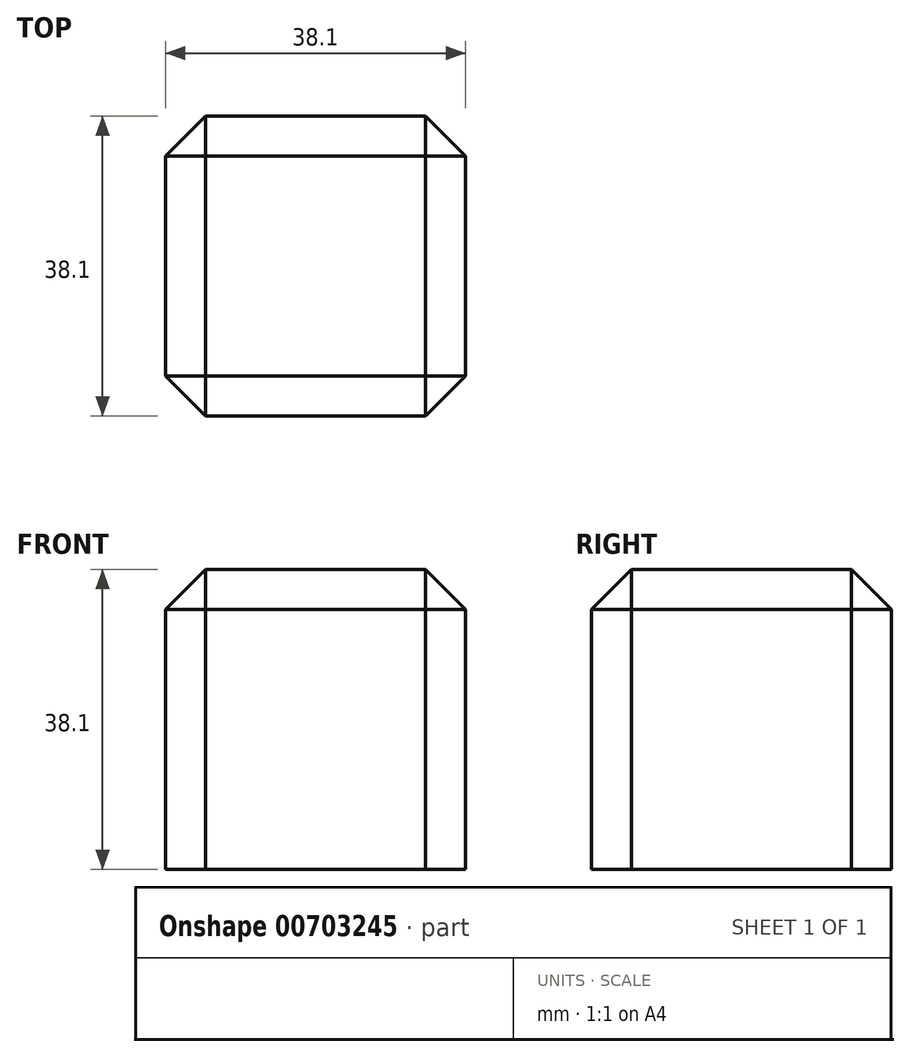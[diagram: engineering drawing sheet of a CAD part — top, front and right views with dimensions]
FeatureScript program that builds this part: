
annotation { "Feature Type Name" : "Feature", "Feature Type Description" : "" }
export const myFeature = defineFeature(function(context is Context, id is Id, definition is map)
    precondition{}
    {
        {
            var Q0;
            Q0=qCreatedBy(makeId("Front.planeOp"),FACE);
            var sketch = newSketch(context, id + "F0", { "sketchPlane" : qUnion([Q0])});
            skLineSegment(sketch, "E0.bottom", {"start": v(19.05, 19.05) * mm, "end": v(-19.05, 19.05) * mm});
            skLineSegment(sketch, "E0.top", {"start": v(19.05, -19.05) * mm, "end": v(-19.05, -19.05) * mm});
            skLineSegment(sketch, "E0.left", {"start": v(19.05, 19.05) * mm, "end": v(19.05, -19.05) * mm});
            skLineSegment(sketch, "E0.right", {"start": v(-19.05, 19.05) * mm, "end": v(-19.05, -19.05) * mm});
            skPoint(sketch, "E0.middle", {"position": v(0, 0) * mm});
            skSolve(sketch);
        }
        {
            var Q0;
            Q0=makeQuery(id+"F0.imprint","IMPRINT",FACE,{"disambiguationData":[TD([[makeQuery(id+"F0.imprint","IMPRINT",EDGE,{"derivedFrom":sQuery(id+"F0.wireOp",EDGE,"E0.bottom")}),1.0]])]});
            extrude(context, id + "F1", {"entities" : qUnion([Q0]), "depth" : 38.1 * mm, "offsetDistance" : 25.4 * mm});
        }
        {
            var Q0;
            Q0=makeQuery(id+"F1.opExtrude","CAP_EDGE",EDGE,{"disambiguationData":[OSD([sQuery(id+"F0.wireOp",EDGE,"E0.bottom")])],"isStart":false});
            var Q1;
            Q1=makeQuery(id+"F1.opExtrude","SWEPT_EDGE",EDGE,{"disambiguationData":[OSD([sQuery(id+"F0.wireOp",EDGE,"E0.bottom"),sQuery(id+"F0.wireOp",EDGE,"E0.right")])]});
            var Q2;
            Q2=makeQuery(id+"F1.opExtrude","CAP_EDGE",EDGE,{"disambiguationData":[OSD([sQuery(id+"F0.wireOp",EDGE,"E0.bottom")])],"isStart":true});
            var Q3;
            Q3=makeQuery(id+"F1.opExtrude","SWEPT_EDGE",EDGE,{"disambiguationData":[OSD([sQuery(id+"F0.wireOp",EDGE,"E0.bottom"),sQuery(id+"F0.wireOp",EDGE,"E0.left")])]});
            var Q4;
            Q4=makeQuery(id+"F1.opExtrude","CAP_EDGE",EDGE,{"disambiguationData":[OSD([sQuery(id+"F0.wireOp",EDGE,"E0.left")])],"isStart":false});
            var Q5;
            Q5=makeQuery(id+"F1.opExtrude","CAP_EDGE",EDGE,{"disambiguationData":[OSD([sQuery(id+"F0.wireOp",EDGE,"E0.left")])],"isStart":true});
            var Q6;
            Q6=makeQuery(id+"F1.opExtrude","CAP_EDGE",EDGE,{"disambiguationData":[OSD([sQuery(id+"F0.wireOp",EDGE,"E0.right")])],"isStart":false});
            var Q7;
            Q7=makeQuery(id+"F1.opExtrude","CAP_EDGE",EDGE,{"disambiguationData":[OSD([sQuery(id+"F0.wireOp",EDGE,"E0.right")])],"isStart":true});
            chamfer(context, id + "F2", {"entities" : qUnion([Q0, Q1, Q2, Q3, Q4, Q5, Q6, Q7]), "width" : 5.08 * mm, "tangentPropagation" : true});
        }
    });
